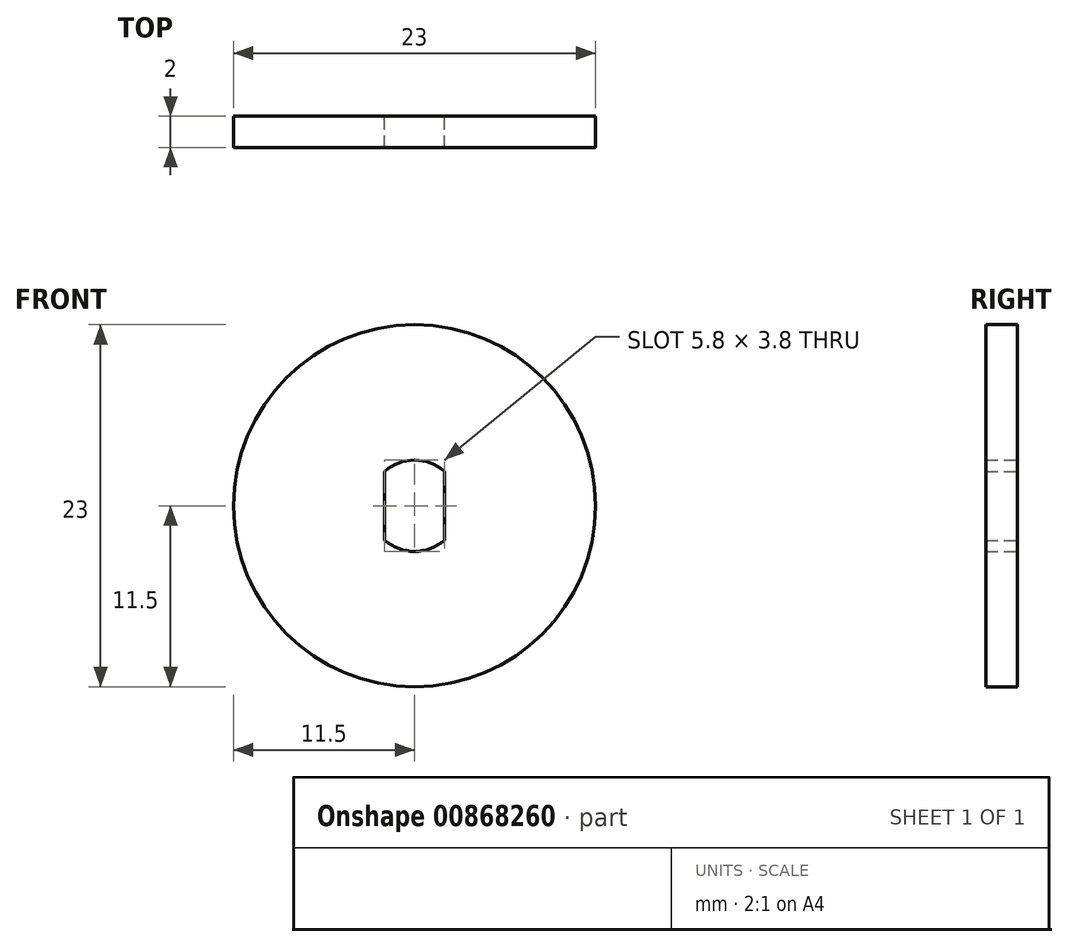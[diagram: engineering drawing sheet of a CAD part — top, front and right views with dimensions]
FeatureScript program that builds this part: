
annotation { "Feature Type Name" : "Feature", "Feature Type Description" : "" }
export const myFeature = defineFeature(function(context is Context, id is Id, definition is map)
    precondition{}
    {
        {
            var Q0;
            Q0=qCreatedBy(makeId("Front.planeOp"),FACE);
            var sketch = newSketch(context, id + "F0", { "sketchPlane" : qUnion([Q0])});
            skCircle(sketch, "E0", {"center": v(0, 0) * mm, "radius": 2.9 * mm});
            skCircle(sketch, "E1", {"center": v(0, 0) * mm, "radius": 11.5 * mm});
            skLineSegment(sketch, "E2", {"start": v(-8, 0) * mm, "end": v(0, 0) * mm, "construction": true});
            skLineSegment(sketch, "E3", {"start": v(0, 0) * mm, "end": v(8, 0) * mm, "construction": true});
            skLineSegment(sketch, "E4.bottom", {"start": v(1.9, 2.2) * mm, "end": v(-1.9, 2.2) * mm});
            skLineSegment(sketch, "E4.top", {"start": v(1.9, -2.2) * mm, "end": v(-1.9, -2.2) * mm});
            skLineSegment(sketch, "E4.left", {"start": v(1.9, 2.2) * mm, "end": v(1.9, -2.2) * mm});
            skLineSegment(sketch, "E4.right", {"start": v(-1.9, 2.2) * mm, "end": v(-1.9, -2.2) * mm});
            skSolve(sketch);
        }
        {
            var Q0;
            Q0=makeQuery(id+"F0.imprint","IMPRINT",FACE,{"disambiguationData":[TD([[makeQuery(id+"F0.imprint","IMPRINT",EDGE,{"derivedFrom":sQuery(id+"F0.wireOp",EDGE,"90f0c5b4-401d-4c3c-840e-b9243e686b54")}),1.0]])]});
            var Q1;
            {var subQ0=sQuery(id+"F0.wireOp",EDGE,"1e8cedca-056d-4308-bc52-5bcca275de9f");Q1=makeQuery(id+"F0.imprint","IMPRINT",FACE,{"disambiguationData":[TD([[makeQuery(id+"F0.imprint","IMPRINT",EDGE,{"derivedFrom":subQ0}),1.0]])]});}
            var Q2;
            {var subQ0=sQuery(id+"F0.wireOp",EDGE,"abda47cd-8e49-40fa-97a4-cba7a21ee996");Q2=makeQuery(id+"F0.imprint","IMPRINT",FACE,{"disambiguationData":[TD([[makeQuery(id+"F0.imprint","IMPRINT",EDGE,{"derivedFrom":subQ0}),1.0]])]});}
            var Q3;
            {var subQ0=sQuery(id+"F0.wireOp",EDGE,"E4.right");Q3=makeQuery(id+"F0.imprint","IMPRINT",FACE,{"disambiguationData":[TD([[makeQuery(id+"F0.imprint","IMPRINT",EDGE,{"derivedFrom":subQ0}),-1.0]])]});}
            var Q4;
            {var subQ0=sQuery(id+"F0.wireOp",EDGE,"E4.left");Q4=makeQuery(id+"F0.imprint","IMPRINT",FACE,{"disambiguationData":[TD([[makeQuery(id+"F0.imprint","IMPRINT",EDGE,{"derivedFrom":subQ0}),1.0]])]});}
            extrude(context, id + "F1", {"entities" : qUnion([Q0, Q1, Q2, Q3, Q4]), "depth" : 2 * mm, "offsetDistance" : 25 * mm});
        }
        {
            var Q0;
            Q0=qSketchRegion(id+"F0",true);
            extrude(context, id + "F2", {"entities" : qUnion([Q0]), "operationType" : NewBodyOperationType.ADD, "depth" : 2 * mm});
        }
    });
